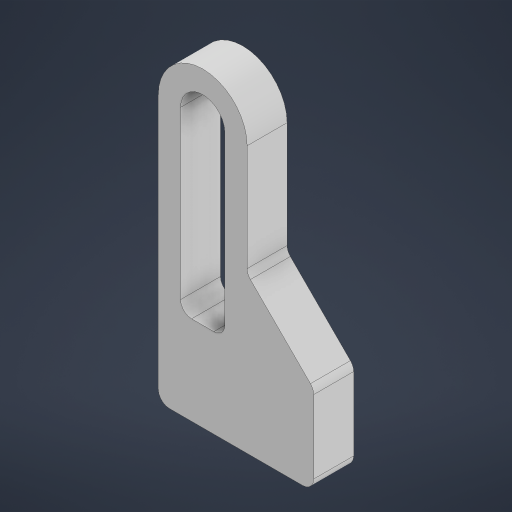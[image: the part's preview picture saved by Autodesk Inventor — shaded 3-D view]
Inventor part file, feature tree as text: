
AUTODESK INVENTOR PART (.ipt)
format: ipt  version: 2023 (Build 270158000, 158)  size: 195,072 bytes
history: native  units: mm
features: extrude x1, fillet x1, sketch x1
ambient origin geometry x8: Origin, YZ Plane, XZ Plane, XY Plane, X Axis, Y Axis, Z Axis, Center Point
bodies: Solid1 (feature_tree)
feature tree (3):
  extrude  "Extrusion1"  Depth=120.0mm
  fillet  "Fillet1"  Radius=30.0mm
  sketch  "Sketch1"  dims[d2=30.0mm d8=120.0mm d11=30.0mm d13=30.0mm d15=30.0mm d16=40.0mm d17=20.0mm d20=40.0mm d21=70.0mm d22=80.0mm d23=20.0mm d24=18.0mm d25=0.0mm d26=5.0mm]
